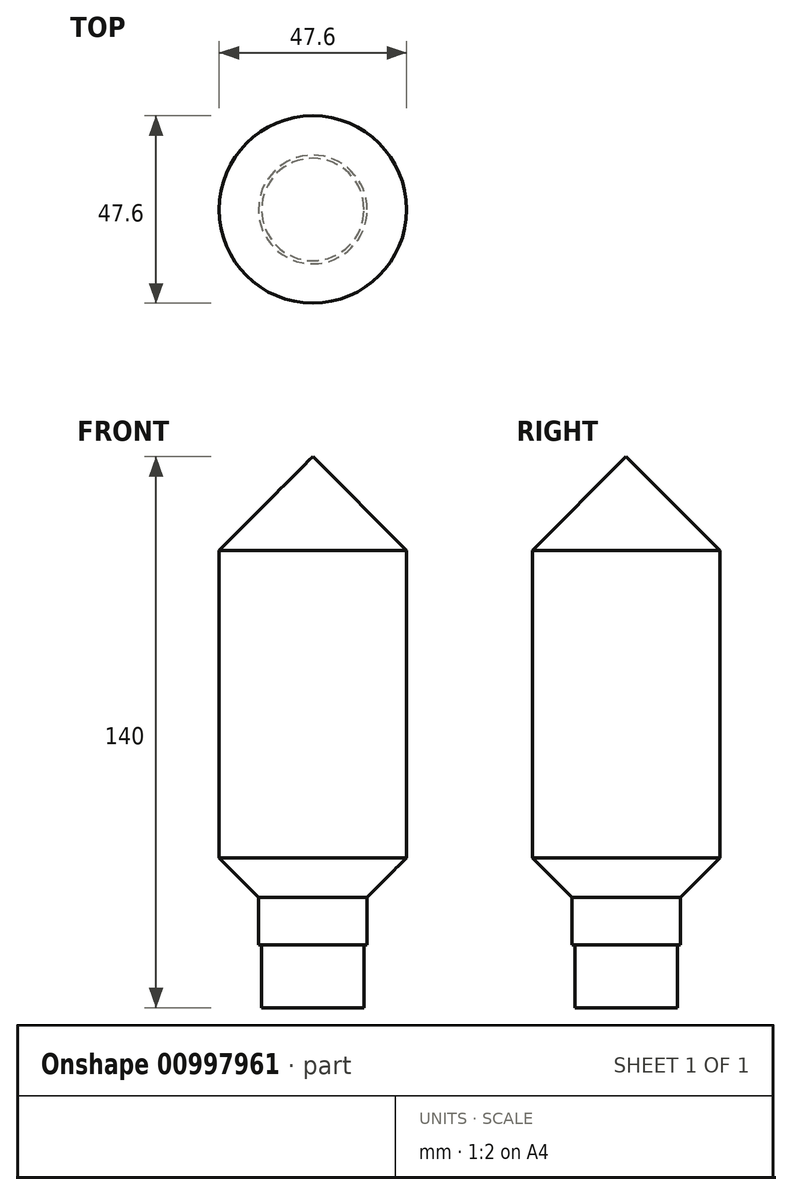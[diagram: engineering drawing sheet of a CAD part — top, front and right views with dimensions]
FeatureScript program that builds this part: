
annotation { "Feature Type Name" : "Feature", "Feature Type Description" : "" }
export const myFeature = defineFeature(function(context is Context, id is Id, definition is map)
    precondition{}
    {
        {
            var Q0;
            Q0=qCreatedBy(makeId("Front.planeOp"),FACE);
            var sketch = newSketch(context, id + "F0", { "sketchPlane" : qUnion([Q0])});
            skLineSegment(sketch, "E0", {"start": v(0, 0) * mm, "end": v(13, 0) * mm});
            skLineSegment(sketch, "E1", {"start": v(13, 0) * mm, "end": v(13, 16) * mm});
            skLineSegment(sketch, "E2", {"start": v(13, 16) * mm, "end": v(13.8, 16) * mm});
            skLineSegment(sketch, "E3", {"start": v(13.8, 16) * mm, "end": v(13.8, 28.07) * mm});
            skLineSegment(sketch, "E4", {"start": v(13.8, 28.07) * mm, "end": v(23.8, 38.07) * mm});
            skLineSegment(sketch, "E5", {"start": v(23.8, 38.07) * mm, "end": v(23.8, 116.2) * mm});
            skLineSegment(sketch, "E6", {"start": v(23.8, 116.2) * mm, "end": v(0, 140) * mm});
            skLineSegment(sketch, "E7", {"start": v(0, 140) * mm, "end": v(0, 0) * mm});
            skLineSegment(sketch, "E8", {"start": v(13.8, 28.07) * mm, "end": v(23.8, 28.07) * mm, "construction": true});
            skLineSegment(sketch, "E9", {"start": v(23.8, 28.07) * mm, "end": v(23.8, 38.07) * mm, "construction": true});
            skLineSegment(sketch, "E10", {"start": v(0, 140) * mm, "end": v(23.8, 140) * mm, "construction": true});
            skLineSegment(sketch, "E11", {"start": v(23.8, 140) * mm, "end": v(23.8, 116.2) * mm, "construction": true});
            skSolve(sketch);
        }
        {
            var Q0;
            Q0=makeQuery(id+"F0.imprint","IMPRINT",FACE,{"disambiguationData":[TD([[makeQuery(id+"F0.imprint","IMPRINT",EDGE,{"derivedFrom":sQuery(id+"F0.wireOp",EDGE,"E0")}),1.0]])]});
            var Q1;
            Q1=sQuery(id+"F0.wireOp",EDGE,"E7");
            revolve(context, id + "F1", {"surfaceOperationType" : NewSurfaceOperationType.NEW, "entities" : qUnion([Q0]), "axis" : qUnion([Q1]), "revolveType" : RevolveType.FULL});
        }
    });
